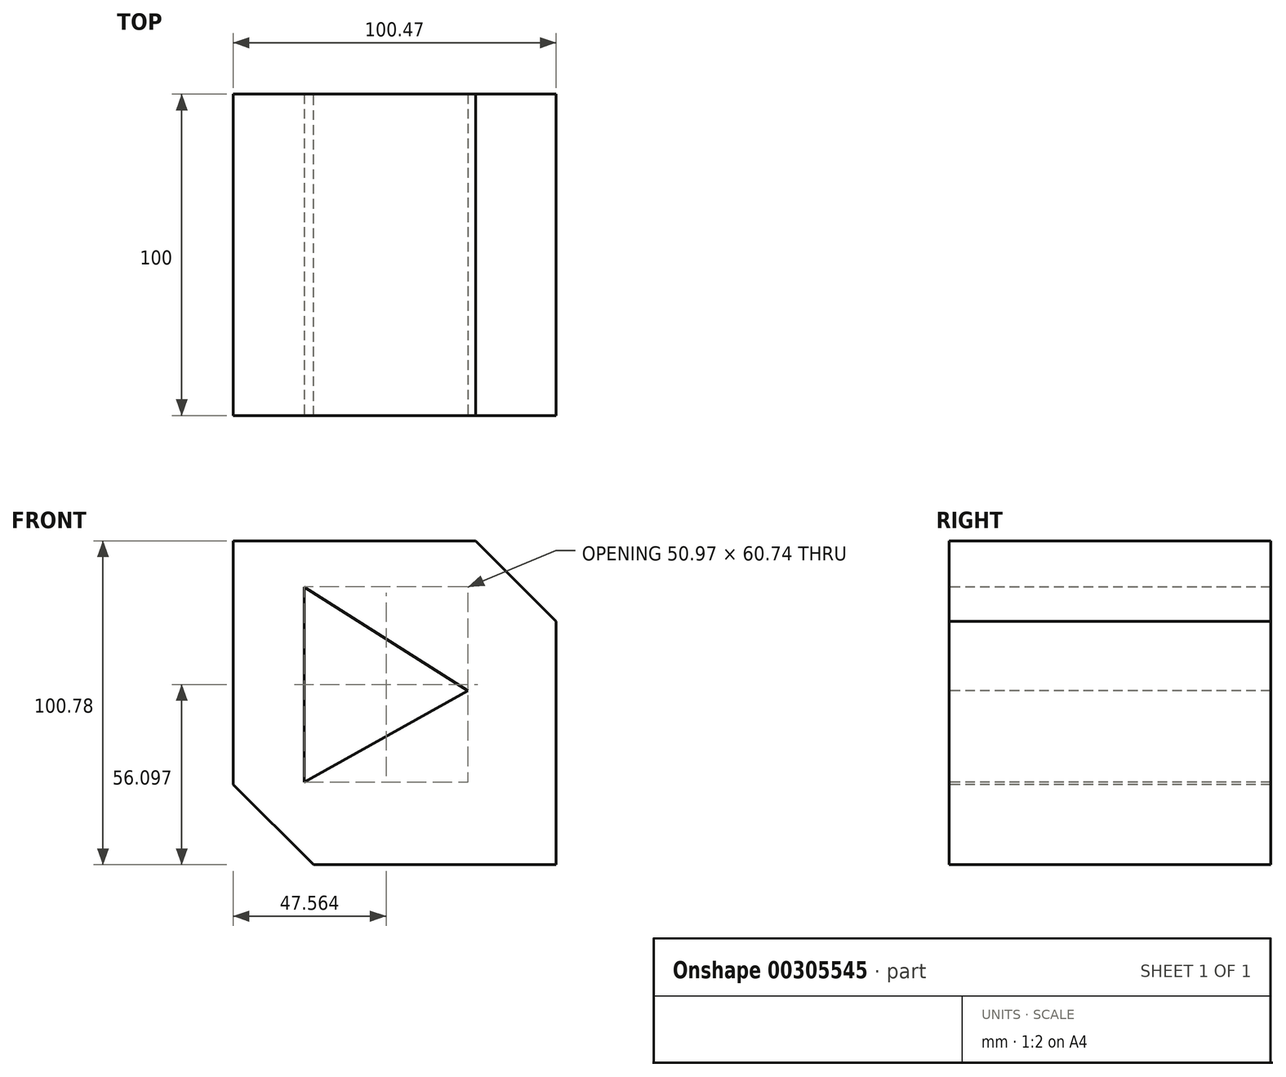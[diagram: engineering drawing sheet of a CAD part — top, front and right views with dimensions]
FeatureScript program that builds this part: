
annotation { "Feature Type Name" : "Feature", "Feature Type Description" : "" }
export const myFeature = defineFeature(function(context is Context, id is Id, definition is map)
    precondition{}
    {
        {
            var Q0;
            Q0=qCreatedBy(makeId("Front.planeOp"),FACE);
            var sketch = newSketch(context, id + "F0", { "sketchPlane" : qUnion([Q0])});
            skLineSegment(sketch, "E0.bottom", {"start": v(-64.81, 36.9) * mm, "end": v(35.66, 36.9) * mm});
            skLineSegment(sketch, "E0.top", {"start": v(-64.81, -63.88) * mm, "end": v(35.66, -63.88) * mm});
            skLineSegment(sketch, "E0.left", {"start": v(-64.81, 36.9) * mm, "end": v(-64.81, -63.88) * mm});
            skLineSegment(sketch, "E0.right", {"start": v(35.66, 36.9) * mm, "end": v(35.66, -63.88) * mm});
            skSolve(sketch);
        }
        {
            var Q0;
            Q0=makeQuery(id+"F0.imprint","IMPRINT",FACE,{"disambiguationData":[TD([[makeQuery(id+"F0.imprint","IMPRINT",EDGE,{"derivedFrom":sQuery(id+"F0.wireOp",EDGE,"E0.bottom")}),-1.0]])]});
            extrude(context, id + "F1", {"entities" : qUnion([Q0]), "depth" : 100 * mm});
        }
        {
            var Q0;
            Q0=makeQuery(id+"F1.opExtrude","SWEPT_EDGE",EDGE,{"disambiguationData":[OSD([sQuery(id+"F0.wireOp",EDGE,"E0.bottom"),sQuery(id+"F0.wireOp",EDGE,"E0.right")])]});
            chamfer(context, id + "F2", {"entities" : qUnion([Q0]), "width" : 25 * mm, "tangentPropagation" : true});
        }
        {
            var Q0;
            Q0=makeQuery(id+"F1.opExtrude","SWEPT_EDGE",EDGE,{"disambiguationData":[OSD([sQuery(id+"F0.wireOp",EDGE,"E0.top"),sQuery(id+"F0.wireOp",EDGE,"E0.left")])]});
            chamfer(context, id + "F3", {"entities" : qUnion([Q0]), "width" : 25 * mm, "tangentPropagation" : true});
        }
        {
            var Q0;
            Q0=makeQuery(id+"F1.opExtrude","CAP_FACE",FACE,{"disambiguationData":[OSD([sQuery(id+"F0.wireOp",EDGE,"E0.bottom"),sQuery(id+"F0.wireOp",EDGE,"E0.top"),sQuery(id+"F0.wireOp",EDGE,"E0.left"),sQuery(id+"F0.wireOp",EDGE,"E0.right")])],"isStart":false});
            var sketch = newSketch(context, id + "F4", { "sketchPlane" : qUnion([Q0])});
            skLineSegment(sketch, "E1", {"start": v(-42.73, -38.15) * mm, "end": v(-42.73, 22.59) * mm});
            skLineSegment(sketch, "E2", {"start": v(-42.73, 22.59) * mm, "end": v(8.24, -9.77) * mm});
            skLineSegment(sketch, "E3", {"start": v(8.24, -9.77) * mm, "end": v(-42.73, -38.15) * mm});
            skSolve(sketch);
        }
        {
            var Q0;
            Q0=makeQuery(id+"F4.imprint","IMPRINT",FACE,{"disambiguationData":[TD([[makeQuery(id+"F4.imprint","IMPRINT",EDGE,{"derivedFrom":sQuery(id+"F4.wireOp",EDGE,"E1")}),-1.0]])]});
            extrude(context, id + "F5", {"entities" : qUnion([Q0]), "operationType" : NewBodyOperationType.REMOVE, "oppositeDirection" : true, "depth" : 100 * mm});
        }
    });
